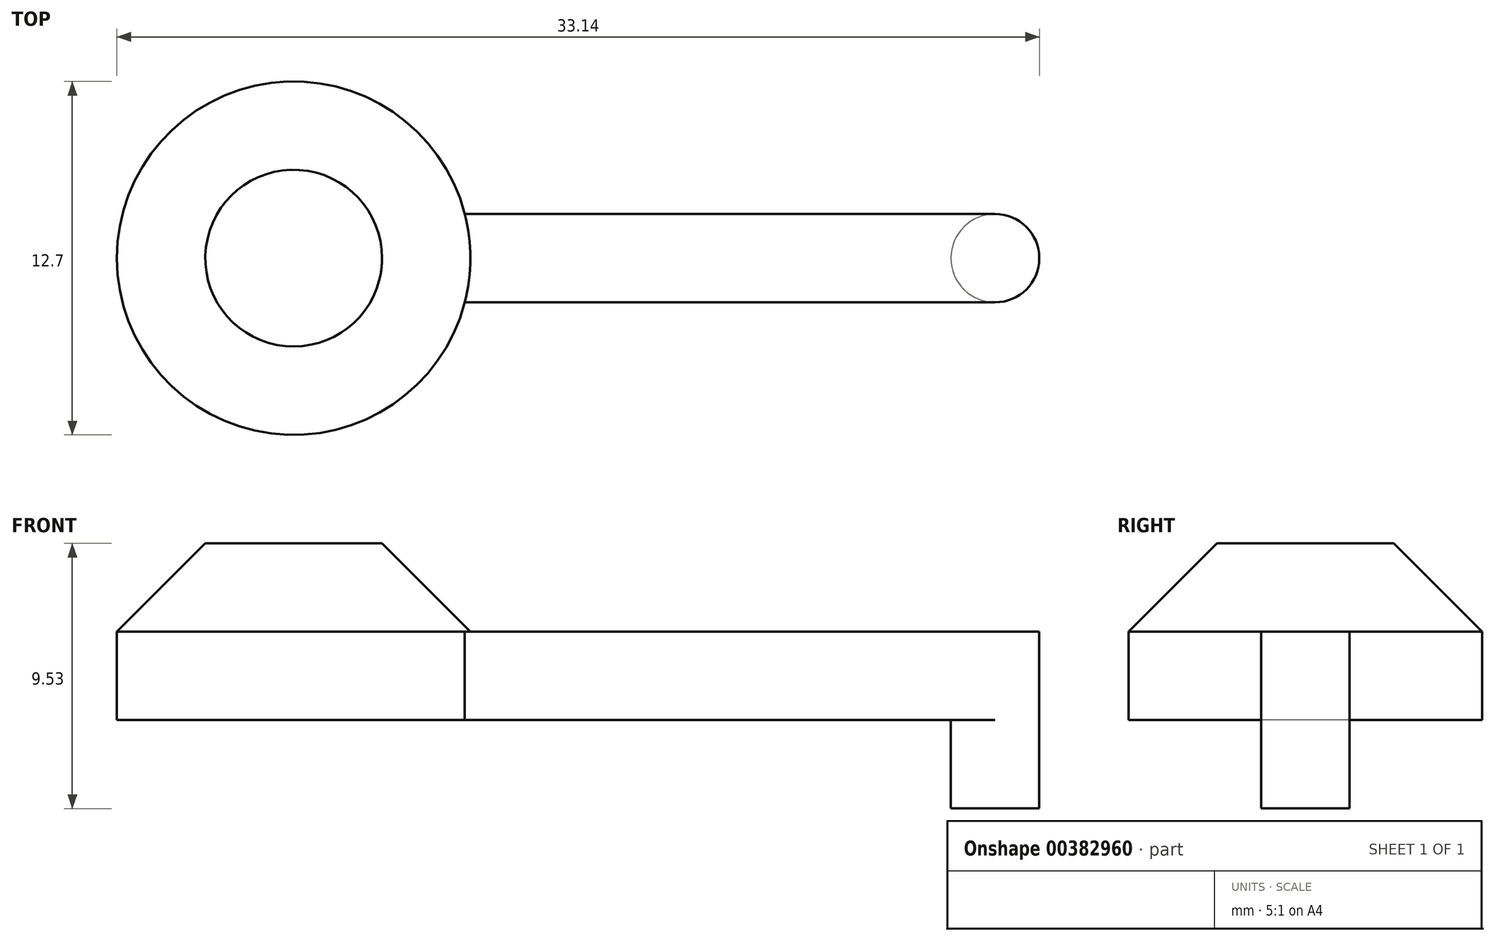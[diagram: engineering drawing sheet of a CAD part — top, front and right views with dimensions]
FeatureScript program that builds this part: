
annotation { "Feature Type Name" : "Feature", "Feature Type Description" : "" }
export const myFeature = defineFeature(function(context is Context, id is Id, definition is map)
    precondition{}
    {
        {
            var Q0;
            Q0=qCreatedBy(makeId("Top.planeOp"),FACE);
            var sketch = newSketch(context, id + "F0", { "sketchPlane" : qUnion([Q0])});
            skCircle(sketch, "E0", {"center": v(0, 0) * mm, "radius": 6.35 * mm});
            skLineSegment(sketch, "E1.bottom", {"start": v(6.15, 1.59) * mm, "end": v(25.2, 1.59) * mm});
            skLineSegment(sketch, "E1.top", {"start": v(6.15, -1.59) * mm, "end": v(25.2, -1.59) * mm});
            skLineSegment(sketch, "E1.left", {"start": v(6.15, 1.59) * mm, "end": v(6.15, -1.59) * mm});
            skLineSegment(sketch, "E1.right", {"start": v(25.2, 1.59) * mm, "end": v(25.2, -1.59) * mm});
            skArc(sketch, "E2", {"start": v(25.2, -1.59) * mm, "mid": v(26.79, 0) * mm, "end": v(25.2, 1.59) * mm});
            skCircle(sketch, "E3", {"center": v(25.2, 0) * mm, "radius": 1.59 * mm});
            skLineSegment(sketch, "E4", {"start": v(0, 0) * mm, "end": v(6.15, 0) * mm});
            skSolve(sketch);
        }
        {
            var Q0;
            {var subQ0=sQuery(id+"F0.wireOp",EDGE,"E1.left");Q0=makeQuery(id+"F0.imprint","IMPRINT",FACE,{"disambiguationData":[TD([[makeQuery(id+"F0.imprint","IMPRINT",EDGE,{"derivedFrom":subQ0}),-1.0]])]});}
            var Q1;
            {var subQ0=sQuery(id+"F0.wireOp",EDGE,"E1.left");Q1=makeQuery(id+"F0.imprint","IMPRINT",FACE,{"disambiguationData":[TD([[makeQuery(id+"F0.imprint","IMPRINT",EDGE,{"derivedFrom":subQ0}),1.0]])]});}
            extrude(context, id + "F1", {"entities" : qUnion([Q0, Q1]), "depth" : 6.35 * mm});
        }
        {
            var Q0;
            {var subQ2=sQuery(id+"F0.wireOp",EDGE,"E1.bottom");Q0=makeQuery(id+"F0.imprint","IMPRINT",FACE,{"disambiguationData":[TD([[makeQuery(id+"F0.imprint","IMPRINT",EDGE,{"derivedFrom":subQ2}),-1.0]])]});}
            var Q1;
            {var subQ0=sQuery(id+"F0.wireOp",EDGE,"E2");Q1=makeQuery(id+"F0.imprint","IMPRINT",FACE,{"disambiguationData":[TD([[makeQuery(id+"F0.imprint","IMPRINT",EDGE,{"derivedFrom":subQ0}),1.0]])]});}
            var Q2;
            {var subQ0=sQuery(id+"F0.wireOp",EDGE,"E3");var subQ1=sQuery(id+"F0.wireOp",EDGE,"E1.right");var subQ2=makeQuery(id+"F0.imprint","INTERSECT",VERTEX,{"disambiguationData":[OD(0.0)],"derivedFrom":[subQ1,subQ0]});Q2=makeQuery(id+"F0.imprint","IMPRINT",FACE,{"disambiguationData":[TD([[makeQuery(id+"F0.imprint","IMPRINT",EDGE,{"disambiguationData":[TD([[subQ2,-1.0]])],"derivedFrom":subQ1}),-1.0]])]});}
            var Q3;
            {var subQ0=sQuery(id+"F0.wireOp",EDGE,"E3");var subQ1=sQuery(id+"F0.wireOp",EDGE,"E1.right");var subQ2=makeQuery(id+"F0.imprint","INTERSECT",VERTEX,{"disambiguationData":[OD(0.0)],"derivedFrom":[subQ1,subQ0]});Q3=makeQuery(id+"F0.imprint","IMPRINT",FACE,{"disambiguationData":[TD([[makeQuery(id+"F0.imprint","IMPRINT",EDGE,{"disambiguationData":[TD([[subQ2,-1.0]])],"derivedFrom":subQ1}),1.0]])]});}
            extrude(context, id + "F2", {"entities" : qUnion([Q0, Q1, Q2, Q3]), "operationType" : NewBodyOperationType.ADD, "depth" : 3.17 * mm});
        }
        {
            var Q0;
            Q0=makeQuery(id+"F1.opExtrude","CAP_EDGE",EDGE,{"disambiguationData":[OSD([sQuery(id+"F0.wireOp",EDGE,"E0")])],"isStart":false});
            chamfer(context, id + "F3", {"entities" : qUnion([Q0]), "width" : 3.17 * mm, "tangentPropagation" : true});
        }
        {
            var Q0;
            {var subQ0=sQuery(id+"F0.wireOp",EDGE,"E3");var subQ1=sQuery(id+"F0.wireOp",EDGE,"E1.right");var subQ2=makeQuery(id+"F0.imprint","INTERSECT",VERTEX,{"disambiguationData":[OD(0.0)],"derivedFrom":[subQ1,subQ0]});Q0=makeQuery(id+"F0.imprint","IMPRINT",FACE,{"disambiguationData":[TD([[makeQuery(id+"F0.imprint","IMPRINT",EDGE,{"disambiguationData":[TD([[subQ2,-1.0]])],"derivedFrom":subQ1}),1.0]])]});}
            var Q1;
            {var subQ0=sQuery(id+"F0.wireOp",EDGE,"E3");var subQ1=sQuery(id+"F0.wireOp",EDGE,"E1.right");var subQ2=makeQuery(id+"F0.imprint","INTERSECT",VERTEX,{"disambiguationData":[OD(0.0)],"derivedFrom":[subQ1,subQ0]});Q1=makeQuery(id+"F0.imprint","IMPRINT",FACE,{"disambiguationData":[TD([[makeQuery(id+"F0.imprint","IMPRINT",EDGE,{"disambiguationData":[TD([[subQ2,-1.0]])],"derivedFrom":subQ1}),-1.0]])]});}
            extrude(context, id + "F4", {"entities" : qUnion([Q0, Q1]), "operationType" : NewBodyOperationType.ADD, "oppositeDirection" : true, "depth" : 3.17 * mm});
        }
    });
